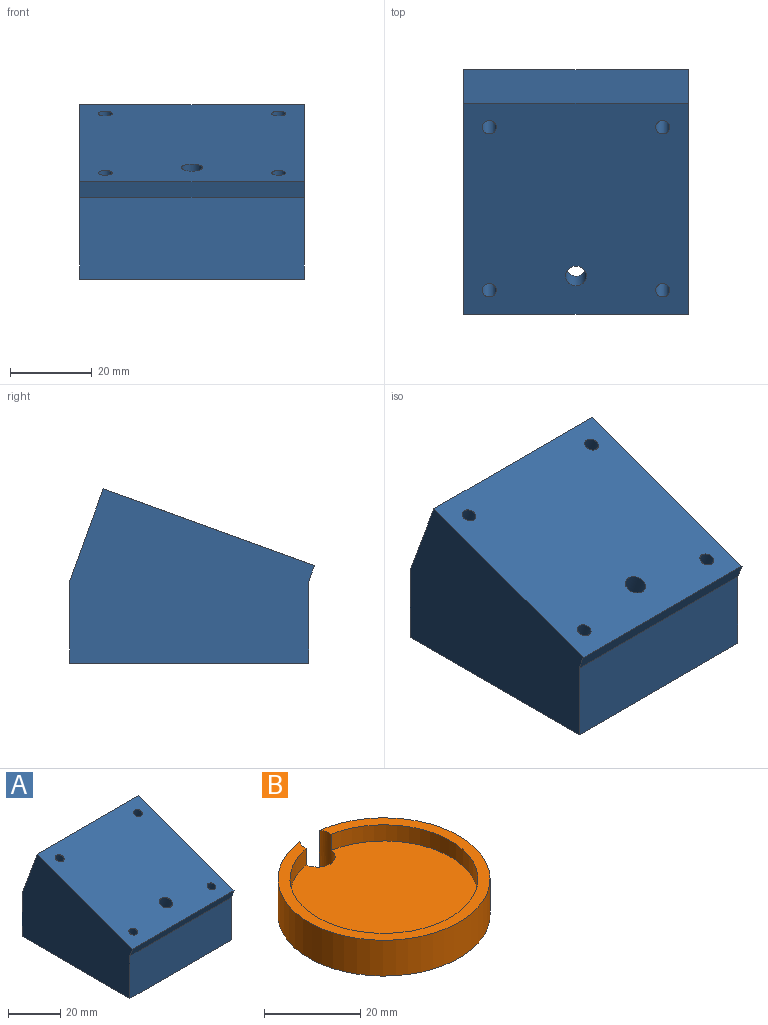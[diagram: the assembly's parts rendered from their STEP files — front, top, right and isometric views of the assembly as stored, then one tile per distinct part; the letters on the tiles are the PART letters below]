
ASSEMBLY  parts=2 mates=1
PART A: 27 faces, bbox 55x59.9x42.7 mm
  f0: plane 55x51.68mm, normal (0,-0.34,0.94), area 2967mm2, adj f1,f2,f3,f4,f11,f13,f15,f17
  f1: plane 55x22.65mm, normal (0,0.94,0.34), area 1325.8mm2, adj f0,f2,f4,f5
  f2: plane 59.93x42.65mm, normal (-1,0,0), area 1945.8mm2, adj f0,f1,f3,f5,f6,f8
  f3: plane 55x3.84mm, normal (0,-0.94,-0.34), area 224.7mm2, adj f0,f2,f4,f6
  f4: plane 59.93x42.65mm, normal (1,0,0), area 1945.8mm2, adj f0,f1,f3,f5,f6,f8
  f5: plane 55x20mm, normal (0,1,0), area 1100mm2, adj f1,f2,f4,f8
  f6: plane 55x20mm, normal (0,-1,0), area 1100mm2, adj f2,f3,f4,f8
  f7: cylinder r=22.5mm len=45mm, axis (0,0,1), area 2827.4mm2, adj f8,f9
  f8: plane 58.53x55mm, normal (0,0,-1), area 1628.7mm2, adj f2,f4,f5,f6,f7
  f9: plane 45x45mm, normal (0,0,-1), area 1518.4mm2, adj f7,f18,f19,f21,f23,f25
  f10: cone r=0mm half-angle=59deg, axis (0,-0.34,0.94), area 10.9mm2, adj f11
  f11: cylinder r=1.73mm len=15.64mm, axis (0,-0.34,0.94), area 166.9mm2, adj f0,f10
  f12: cone r=0mm half-angle=59deg, axis (0,-0.34,0.94), area 10.9mm2, adj f13
  f13: cylinder r=1.73mm len=15.64mm, axis (0,-0.34,0.94), area 166.9mm2, adj f0,f12
  f14: cone r=0mm half-angle=59deg, axis (0,-0.34,0.94), area 10.9mm2, adj f15
  f15: cylinder r=1.73mm len=15.64mm, axis (0,-0.34,0.94), area 166.9mm2, adj f0,f14
  f16: cone r=0mm half-angle=59deg, axis (0,-0.34,0.94), area 10.9mm2, adj f17
  f17: cylinder r=1.73mm len=15.64mm, axis (0,-0.34,0.94), area 166.9mm2, adj f0,f16
  f18: cylinder r=2.55mm len=9.89mm, axis (0,-0.34,0.94), area 123.9mm2, adj f0,f9
  f19: cylinder r=2mm len=8mm, axis (0,0,1), area 100.5mm2, adj f9,f20
  f20: plane 4x4mm, normal (0,0,-1), area 12.6mm2, adj f19
  f21: cylinder r=2mm len=8mm, axis (0,0,1), area 100.5mm2, adj f9,f22
  f22: plane 4x4mm, normal (0,0,-1), area 12.6mm2, adj f21
  f23: cylinder r=2mm len=8mm, axis (0,0,1), area 100.5mm2, adj f9,f24
  f24: plane 4x4mm, normal (0,0,-1), area 12.6mm2, adj f23
  f25: cylinder r=2mm len=8mm, axis (0,0,1), area 100.5mm2, adj f9,f26
  f26: plane 4x4mm, normal (0,0,-1), area 12.6mm2, adj f25
PART B: 6 faces, bbox 44x43.8x9.1 mm
  f0: cylinder r=22mm len=44mm, axis (0,0,-1), area 1205.5mm2, adj f1,f3,f5
  f1: cylinder r=3.68mm len=9.1mm, axis (0,0,-1), area 106.2mm2, adj f0,f2,f3,f4,f5
  f2: cylinder r=19.5mm len=39mm, axis (0,0,-1), area 472.1mm2, adj f1,f3,f4
  f3: plane 44x43.81mm, normal (0,0,1), area 308.5mm2, adj f0,f1,f2
  f4: plane 39x38.65mm, normal (0,0,1), area 1174.1mm2, adj f1,f2
  f5: plane 44x43.81mm, normal (0,0,-1), area 1482.7mm2, adj f0,f1
PLACE A t=(-0.51,-3.13,-6.63)mm
PLACE B rot(axis=(1,0,0),180deg) t=(-0.51,-3.13,-19.63)mm
MATE fastened B.f0 <-> A.f7  axis (0,0,1) through (-0.51,-3.13,-14.63)mm
